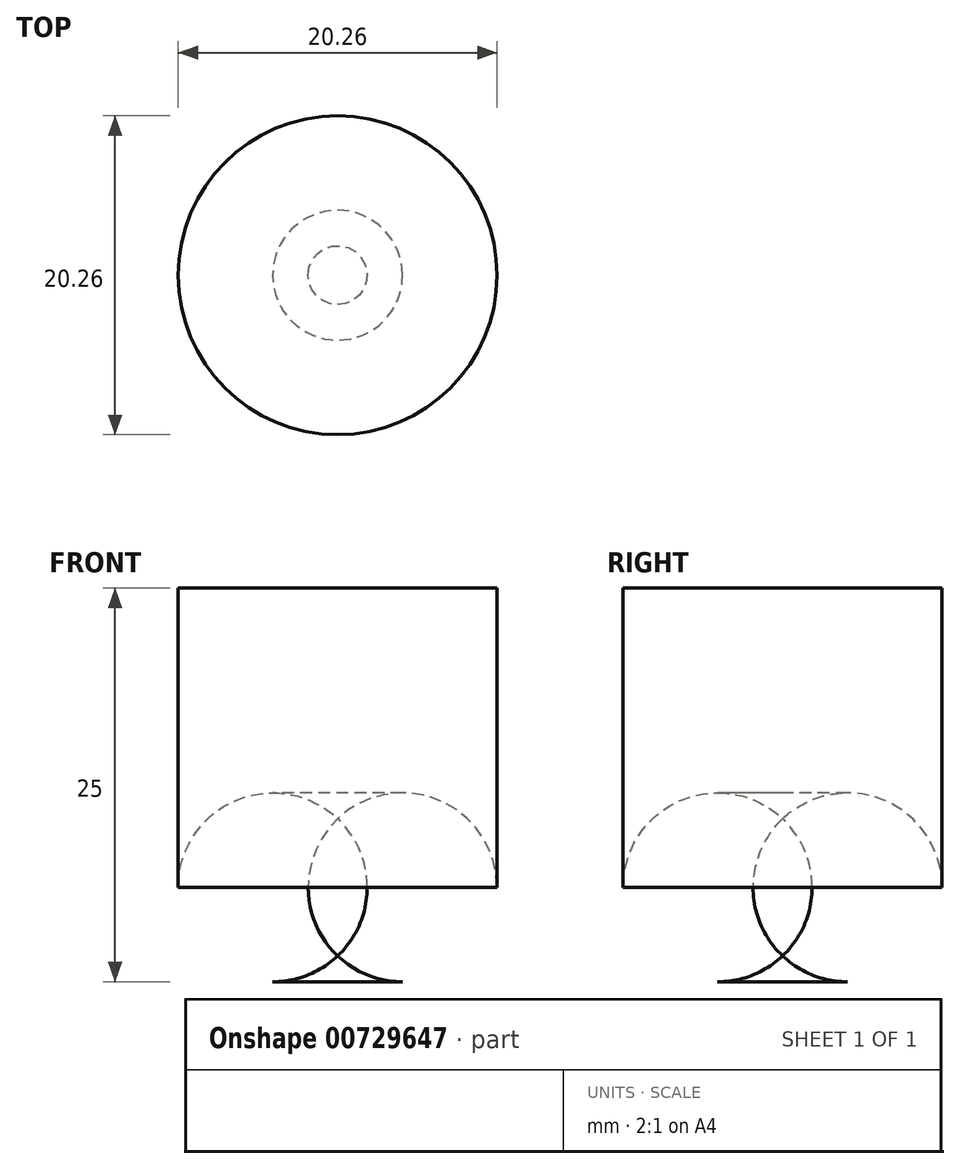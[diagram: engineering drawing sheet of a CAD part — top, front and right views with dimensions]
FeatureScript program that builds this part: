
annotation { "Feature Type Name" : "Feature", "Feature Type Description" : "" }
export const myFeature = defineFeature(function(context is Context, id is Id, definition is map)
    precondition{}
    {
        {
            var Q0;
            Q0=qCreatedBy(makeId("Front.planeOp"),FACE);
            var sketch = newSketch(context, id + "F0", { "sketchPlane" : qUnion([Q0])});
            skLineSegment(sketch, "E0", {"start": v(0, 26.77) * mm, "end": v(0, -46.83) * mm, "construction": true});
            skLineSegment(sketch, "E1", {"start": v(0, 25) * mm, "end": v(10.13, 25) * mm});
            skLineSegment(sketch, "E2", {"start": v(10.12, 25) * mm, "end": v(10.12, 6) * mm});
            skLineSegment(sketch, "E3", {"start": v(4.13, 0) * mm, "end": v(0, 0) * mm});
            skPoint(sketch, "E4.visualSharp", {"position": v(10.12, 0) * mm});
            skArc(sketch, "E4.filletArc", {"start": v(4.13, 0) * mm, "mid": v(8.37, 1.76) * mm, "end": v(10.13, 6) * mm});
            skLineSegment(sketch, "E5", {"start": v(0, 25) * mm, "end": v(0, 0) * mm});
            skSolve(sketch);
        }
        {
            var Q0;
            Q0=makeQuery(id+"F0.imprint","IMPRINT",FACE,{"disambiguationData":[TD([[makeQuery(id+"F0.imprint","IMPRINT",EDGE,{"derivedFrom":sQuery(id+"F0.wireOp",EDGE,"E1")}),-1.0]])]});
            var Q1;
            Q1=sQuery(id+"F0.wireOp",EDGE,"E0");
            revolve(context, id + "F1", {"surfaceOperationType" : NewSurfaceOperationType.NEW, "entities" : qUnion([Q0]), "axis" : qUnion([Q1]), "revolveType" : RevolveType.FULL});
        }
    });
